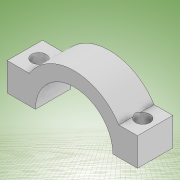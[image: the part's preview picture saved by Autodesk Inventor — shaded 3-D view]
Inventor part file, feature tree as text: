
AUTODESK INVENTOR PART (.ipt)
format: ipt  version: 2022 (Build 260153000, 153)  size: 141,824 bytes
history: native  units: mm
features: extrude x2, sketch x2, other x1
ambient origin geometry x8: Origin, YZ Plane, XZ Plane, XY Plane, X Axis, Y Axis, Z Axis, Center Point
bodies: Body1 (feature_tree)
feature tree (5):
  other  "Sólido1"
  extrude  "Extrusión1"  Depth=37.0mm
  extrude  "Extrusión3"  Depth=8.0mm
  sketch  "Boceto1"  dims[d0=11.0mm d1=37.0mm]
  sketch  "Boceto3"  dims[d2=8.0mm d3=8.0mm d5=4.0mm d6=10.0mm d7=0.0mm d12=4.1mm d13=4.1mm d14=0.0mm d15=0.0mm]
